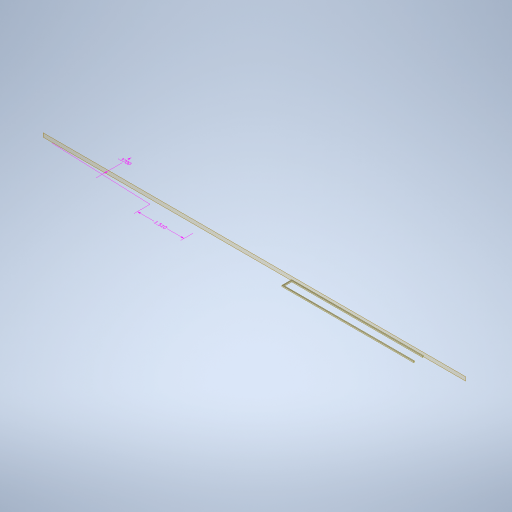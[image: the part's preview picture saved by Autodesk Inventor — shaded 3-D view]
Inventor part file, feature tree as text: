
AUTODESK INVENTOR PART (.ipt)
format: ipt  version: 2024.2 (Build 282272000, 272)  size: 277,504 bytes
history: native  units: in
note: dims shown in document units (in); Inventor stores cm internally (conversion verified against a paired STEP export)
features: other x3, plane x3, sketch x2, sweep x1
ambient origin geometry x8: Origin, YZ Plane, XZ Plane, XY Plane, X Axis, Y Axis, Z Axis, Center Point
bodies: Solid1 (feature_tree)
feature tree (9):
  other  "Annotations"
  sweep  "Sweep1"
  plane  "Work Plane1"
  plane  "Work Plane2"
  plane  "Work Plane4"
  sketch  "Sketch1"  dims[d6=0.0in d7=0.0in d11=0.25in d19=-0.25in]
  sketch  "Sketch2"  dims[d69=1.325in d70=1.325in d86=-0.1175in d89=0.1in d90=0.0in d91=0.0in d92=0.0in d98=0.01in d99=0.01in d42=0.2341in d43=0.169in d44=0.37in d48=0.2141in d49=0.2512in d50=1.51in]
  other  "Linear Dimension 1"
  other  "Linear Dimension 3"
